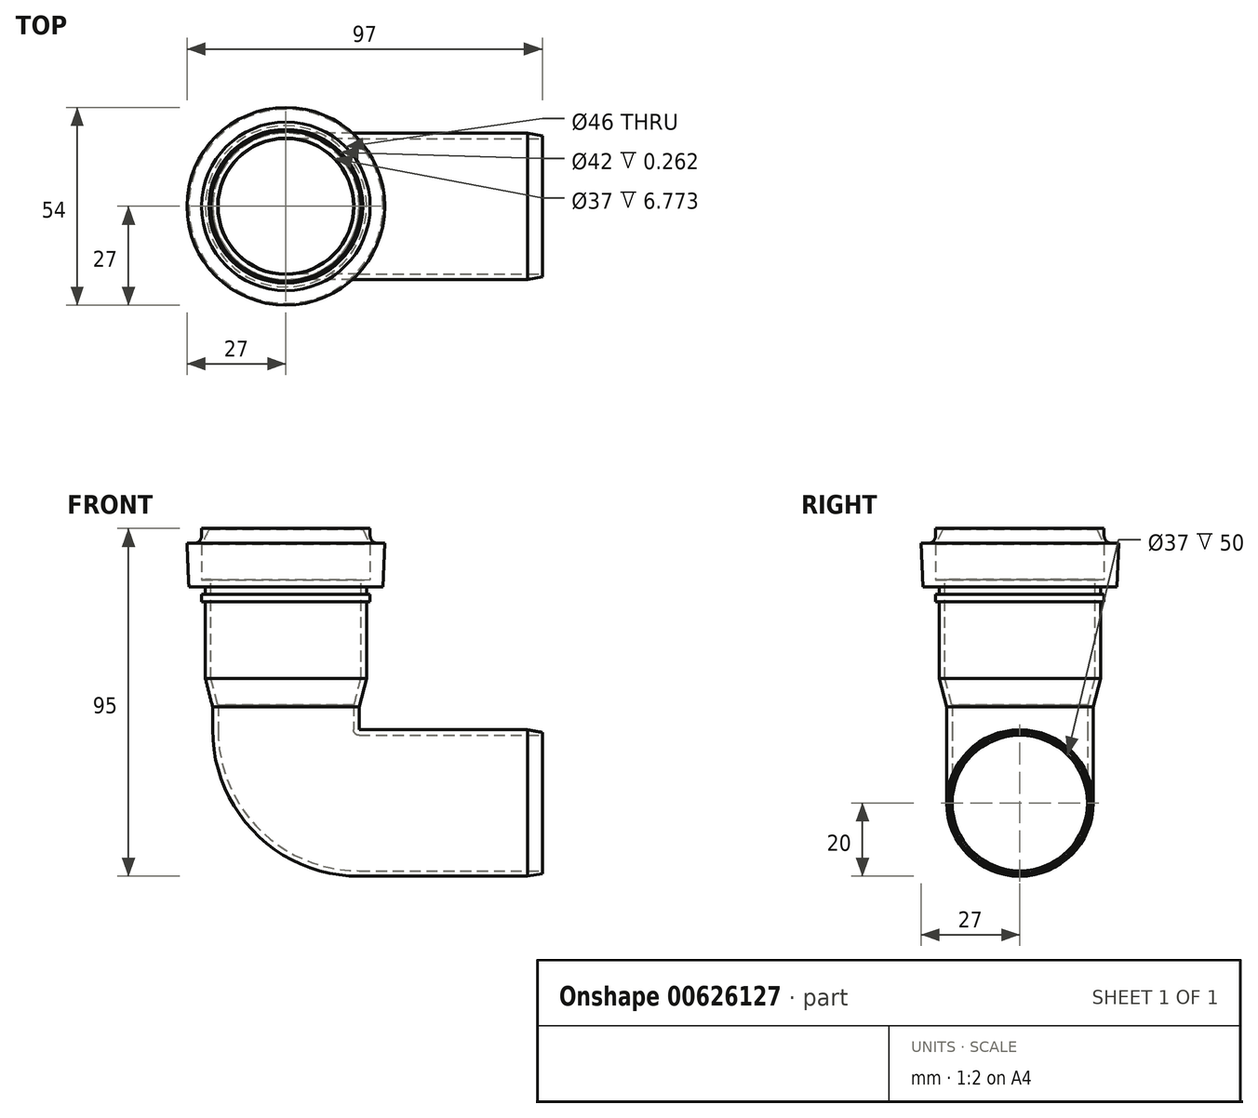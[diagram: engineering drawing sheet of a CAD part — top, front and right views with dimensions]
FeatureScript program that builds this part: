
annotation { "Feature Type Name" : "Feature", "Feature Type Description" : "" }
export const myFeature = defineFeature(function(context is Context, id is Id, definition is map)
    precondition{}
    {
        {
            var Q0;
            Q0=qCreatedBy(makeId("Front.planeOp"),FACE);
            var sketch = newSketch(context, id + "F0", { "sketchPlane" : qUnion([Q0])});
            skLineSegment(sketch, "E0", {"start": v(0, -34.29) * mm, "end": v(0, 41.01) * mm});
            skLineSegment(sketch, "E1", {"start": v(-22, 31.74) * mm, "end": v(-22, 10.74) * mm});
            skLineSegment(sketch, "E2", {"start": v(-22, 10.74) * mm, "end": v(-20, 3) * mm});
            skLineSegment(sketch, "E3", {"start": v(-22, 31.74) * mm, "end": v(-23, 31.74) * mm});
            skLineSegment(sketch, "E4", {"start": v(-23, 31.74) * mm, "end": v(-23, 33.74) * mm});
            skLineSegment(sketch, "E5", {"start": v(-23, 33.74) * mm, "end": v(-22, 33.74) * mm});
            skLineSegment(sketch, "E6", {"start": v(-22, 33.74) * mm, "end": v(-22, 35.74) * mm});
            skLineSegment(sketch, "E7", {"start": v(-22, 35.74) * mm, "end": v(-26.5, 35.74) * mm});
            skLineSegment(sketch, "E8", {"start": v(-26.5, 35.74) * mm, "end": v(-27, 47.73) * mm});
            skLineSegment(sketch, "E9", {"start": v(-27, 47.73) * mm, "end": v(-25, 47.73) * mm});
            skLineSegment(sketch, "E10", {"start": v(-23, 49.73) * mm, "end": v(-23, 51.73) * mm});
            skLineSegment(sketch, "E11", {"start": v(-23, 51.73) * mm, "end": v(-21, 51.73) * mm});
            skLineSegment(sketch, "E12", {"start": v(-23, 37.74) * mm, "end": v(-23, 47.42) * mm});
            skLineSegment(sketch, "E13", {"start": v(-23, 37.74) * mm, "end": v(-20.5, 37.75) * mm});
            skPoint(sketch, "E14.visualSharp", {"position": v(-23, 47.73) * mm});
            skArc(sketch, "E14.filletArc", {"start": v(-25, 47.73) * mm, "mid": v(-23.59, 48.31) * mm, "end": v(-23, 49.73) * mm});
            skLineSegment(sketch, "E15", {"start": v(-20, 3) * mm, "end": v(-18.5, 3) * mm});
            skLineSegment(sketch, "E16", {"start": v(-20.48, 10.78) * mm, "end": v(-20.5, 37.75) * mm});
            skLineSegment(sketch, "E17", {"start": v(-18.5, 3) * mm, "end": v(-20.48, 10.78) * mm});
            skLineSegment(sketch, "E18", {"start": v(-21, 51.73) * mm, "end": v(-21, 51.47) * mm});
            skLineSegment(sketch, "E19", {"start": v(-21, 51.47) * mm, "end": v(-23, 47.42) * mm});
            skSolve(sketch);
        }
        {
            var Q0;
            Q0 = qSketchRegion(id + "F0", true);
            var Q1;
            Q1=sQuery(id+"F0.wireOp",EDGE,"E0");
            revolve(context, id + "F1", {"entities" : qUnion([Q0]), "axis" : qUnion([Q1]), "revolveType" : RevolveType.FULL});
        }
        {
            var Q0;
            Q0=qCreatedBy(makeId("Front.planeOp"),FACE);
            var sketch = newSketch(context, id + "F2", { "sketchPlane" : qUnion([Q0])});
            skLineSegment(sketch, "E20", {"start": v(20, -23.27) * mm, "end": v(70, -23.27) * mm});
            skLineSegment(sketch, "E21", {"start": v(0, -3.27) * mm, "end": v(0, 3.5) * mm});
            skPoint(sketch, "E22.visualSharp", {"position": v(0, -20) * mm});
            skArc(sketch, "E22.filletArc", {"start": v(0, -3.27) * mm, "mid": v(5.86, -17.41) * mm, "end": v(20, -23.27) * mm});
            skSolve(sketch);
        }
        {
            var Q0;
            Q0=makeQuery(id+"F1.opRevolve","SWEPT_FACE",FACE,{"disambiguationData":[OSD([sQuery(id+"F0.wireOp",EDGE,"E15")])]});
            var Q1;
            Q1=sQuery(id+"F2.wireOp",EDGE,"E21");
            var Q2;
            Q2=sQuery(id+"F2.wireOp",EDGE,"E20");
            var Q3;
            Q3=sQuery(id+"F2.wireOp",EDGE,"E22.filletArc");
            sweep(context, id + "F3", {"operationType" : NewBodyOperationType.ADD, "profiles" : qUnion([Q0]), "path" : qUnion([Q1, Q2, Q3])});
        }
        {
            var Q0;
            Q0=makeQuery(id+"F3.opSweep","CAP_EDGE",EDGE,{"disambiguationData":[OSD([sQuery(id+"F0.wireOp",EDGE,"E2"),sQuery(id+"F0.wireOp",EDGE,"E15"),sQuery(id+"F2.wireOp",VERTEX,"E20.end")])],"isStart":false});
            chamfer(context, id + "F4", {"entities" : qUnion([Q0]), "chamferType" : ChamferType.OFFSET_ANGLE, "width" : 4 * mm, "oppositeDirection" : true, "angle" : 10 * degree, "tangentPropagation" : true});
        }
    });
